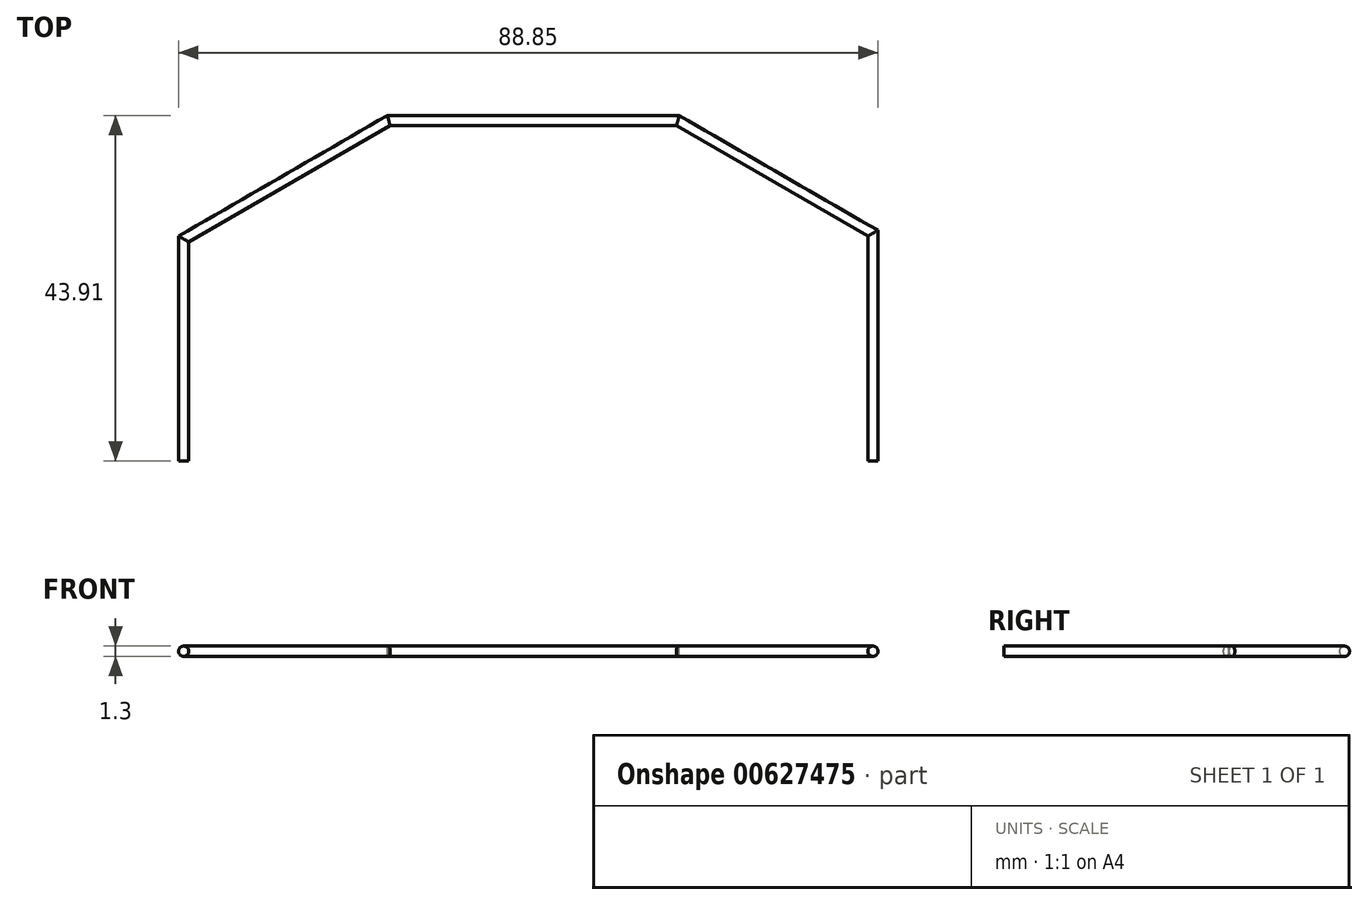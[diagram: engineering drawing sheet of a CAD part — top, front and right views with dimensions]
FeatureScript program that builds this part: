
annotation { "Feature Type Name" : "Feature", "Feature Type Description" : "" }
export const myFeature = defineFeature(function(context is Context, id is Id, definition is map)
    precondition{}
    {
        {
            var Q0;
            Q0=qCreatedBy(makeId("Top.planeOp"),FACE);
            var sketch = newSketch(context, id + "F0", { "sketchPlane" : qUnion([Q0])});
            skLineSegment(sketch, "E0", {"start": v(0, 0) * mm, "end": v(0, 28.21) * mm});
            skLineSegment(sketch, "E1", {"start": v(0, 28.21) * mm, "end": v(26.05, 43.26) * mm});
            skLineSegment(sketch, "E2", {"start": v(26.05, 43.26) * mm, "end": v(62.77, 43.26) * mm});
            skLineSegment(sketch, "E3", {"start": v(62.77, 43.26) * mm, "end": v(87.54, 28.95) * mm});
            skLineSegment(sketch, "E4", {"start": v(87.54, 28.95) * mm, "end": v(87.54, 0) * mm});
            skSolve(sketch);
        }
        {
            var Q0;
            Q0=qCreatedBy(makeId("Front.planeOp"),FACE);
            var sketch = newSketch(context, id + "F1", { "sketchPlane" : qUnion([Q0])});
            skCircle(sketch, "E5", {"center": v(0, 0) * mm, "radius": 0.65 * mm});
            skSolve(sketch);
        }
        {
            var Q0;
            Q0=makeQuery(id+"F1.imprint","IMPRINT",FACE,{"disambiguationData":[TD([[makeQuery(id+"F1.imprint","IMPRINT",EDGE,{"derivedFrom":sQuery(id+"F1.wireOp",EDGE,"E5")}),1.0]])]});
            var Q1;
            Q1=sQuery(id+"F0.wireOp",EDGE,"E0");
            var Q2;
            Q2=sQuery(id+"F0.wireOp",EDGE,"E1");
            var Q3;
            Q3=sQuery(id+"F0.wireOp",EDGE,"E2");
            var Q4;
            Q4=sQuery(id+"F0.wireOp",EDGE,"E3");
            var Q5;
            Q5=sQuery(id+"F0.wireOp",EDGE,"E4");
            sweep(context, id + "F2", {"profiles" : qUnion([Q0]), "path" : qUnion([Q1, Q2, Q3, Q4, Q5])});
        }
    });
